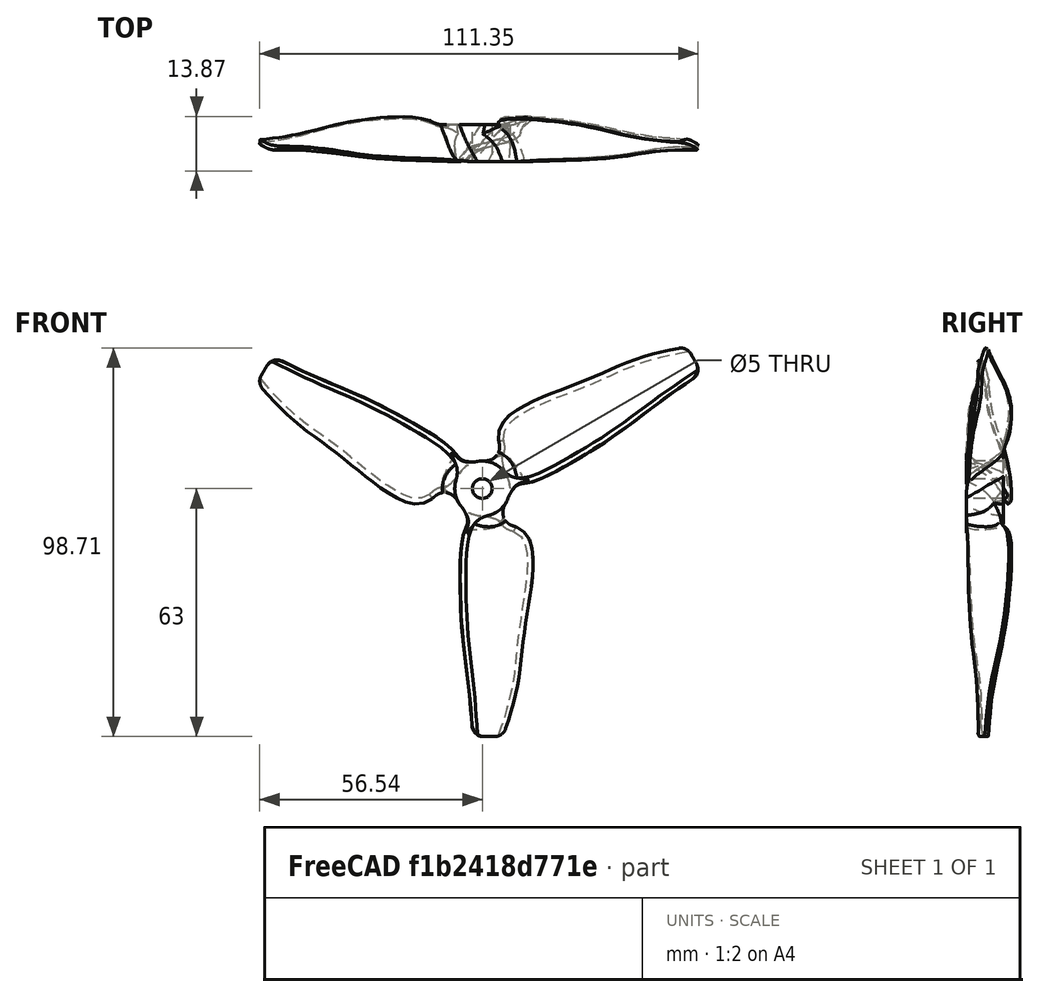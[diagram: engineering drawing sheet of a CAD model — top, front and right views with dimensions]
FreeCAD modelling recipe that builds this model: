
FCSTD DOCUMENT  (FreeCAD 0.18R16033 (Git))
Label: propeller_05
License: All rights reserved
LicenseURL: http://en.wikipedia.org/wiki/All_rights_reserved
objects: Part::Feature×3, PartDesign::ShapeBinder×1, Sketcher::SketchObject×1, PartDesign::Pad×1, PartDesign::Body×1, Part::Fuse×1, App::MeasureDistance×1
note: 9 computed .brp shape members not serialized (recipe doc carries the construction recipe); baked Part::Feature solids carry a one-line shape summary decoded from their .brp

FEATURE [Part::Feature] Part__Feature  label="Propeller_V4 CW v2"
  shape: bbox 119.9 x 15.9 x 107.4 mm, 75 faces (baked)
FEATURE [Part::Feature] Part__Feature001  label="Propeller_V4 CW v003"
  shape: bbox 119.9 x 15.9 x 107.4 mm, 75 faces (baked)
FEATURE [PartDesign::ShapeBinder] CopyPart__Feature001
  TraceSupport = false
FEATURE [Sketcher::SketchObject] Sketch
  MapMode = 5
  Placement = pos=(0,-3.25,0) rot=(1,0,0;1.5708rad)
  Support = -> [CopyPart__Feature001]
  sketch-geometry (1):
    g0: Circle CenterX=0 CenterY=0 CenterZ=0 NormalX=0 NormalY=0 NormalZ=1 AngleXU=0 Radius=4.00121
FEATURE [PartDesign::Pad] Pad
  Length = 9.5
  Length2 = 100
  Profile = -> Sketch
  Reversed = true
  Type = 0
FEATURE [PartDesign::Body] Body
  Group = -> [CopyPart__Feature001,Sketch,Pad]
  Origin = -> Origin
  Tip = -> Pad
FEATURE [Part::Fuse] Fusion
  Base = -> Part__Feature001
  Tool = -> Body
FEATURE [Part::Feature] Fusion001
  shape: bbox 119.9 x 15.9 x 107.4 mm, 74 faces (baked)
FEATURE [App::MeasureDistance] Distance  label="Distance: 61.38 mm"
  Distance = 61.3781
  P1 = (-0.256896,-3.25,-0.066966)
  P2 = (-53.3409,0.201345,30.5508)
